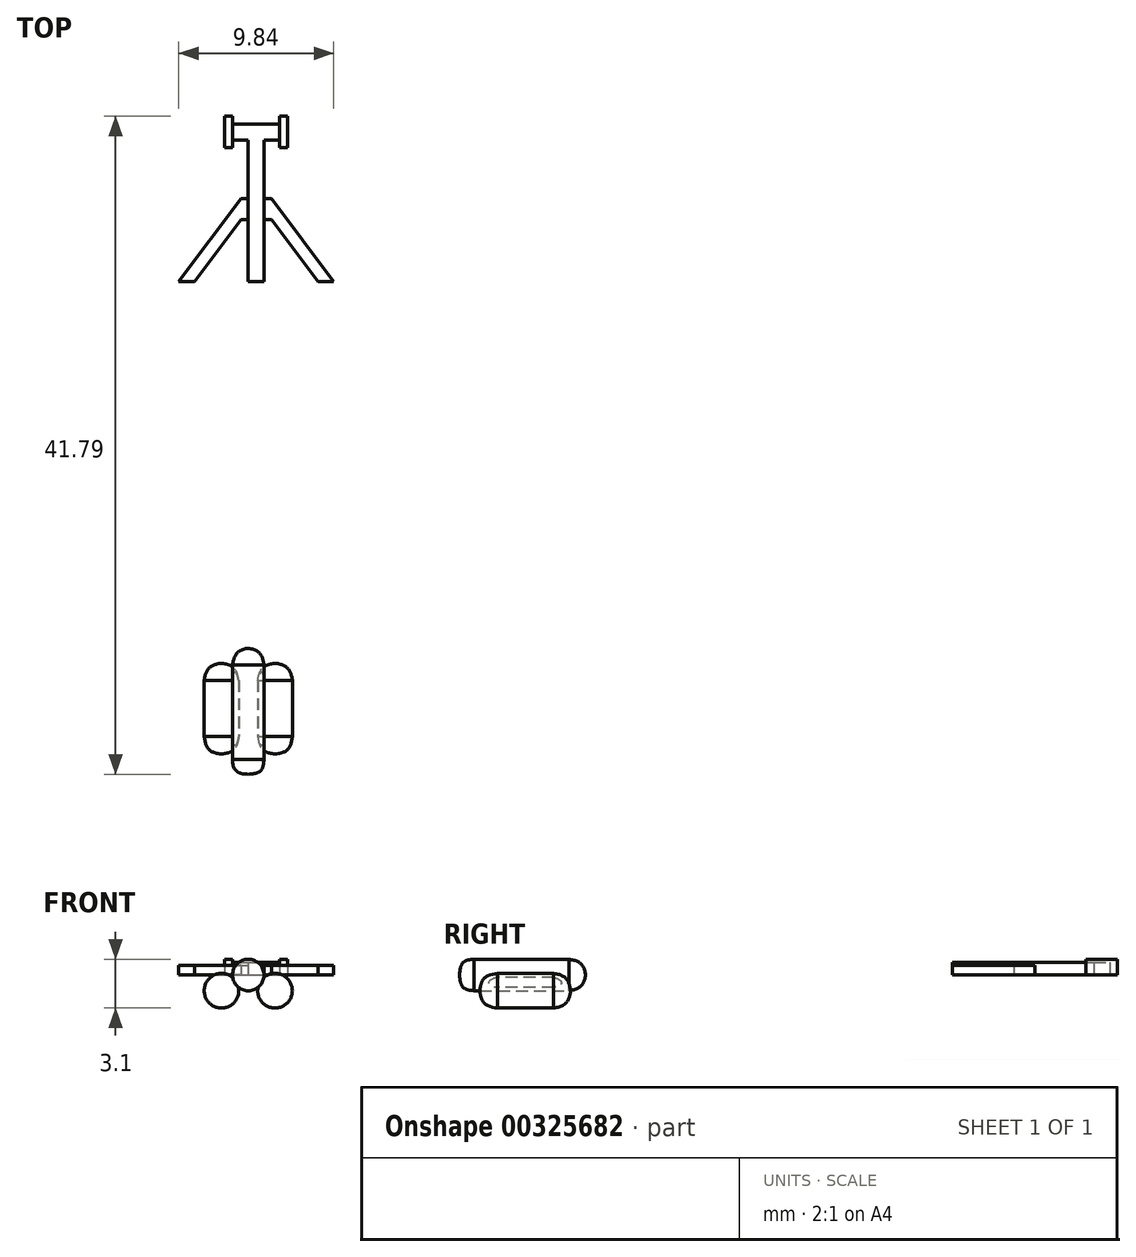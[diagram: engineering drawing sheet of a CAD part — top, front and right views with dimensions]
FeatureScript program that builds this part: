
annotation { "Feature Type Name" : "Feature", "Feature Type Description" : "" }
export const myFeature = defineFeature(function(context is Context, id is Id, definition is map)
    precondition{}
    {
        {
            var Q0;
            Q0=qCreatedBy(makeId("Top.planeOp"),FACE);
            var sketch = newSketch(context, id + "F0", { "sketchPlane" : qUnion([Q0])});
            skLineSegment(sketch, "E0.bottom", {"start": v(0, 0) * mm, "end": v(1, 0) * mm});
            skLineSegment(sketch, "E0.top", {"start": v(0, 10) * mm, "end": v(1, 10) * mm});
            skLineSegment(sketch, "E0.left", {"start": v(0, 0) * mm, "end": v(0, 10) * mm});
            skLineSegment(sketch, "E0.right", {"start": v(1, 0) * mm, "end": v(1, 10) * mm});
            skPoint(sketch, "E1", {"position": v(0.5, 10) * mm});
            skLineSegment(sketch, "E2.bottom", {"start": v(-1, 10) * mm, "end": v(2, 10) * mm});
            skLineSegment(sketch, "E2.top", {"start": v(-1, 9) * mm, "end": v(2, 9) * mm});
            skLineSegment(sketch, "E2.left", {"start": v(2, 10) * mm, "end": v(2, 9) * mm});
            skLineSegment(sketch, "E2.right", {"start": v(-1, 10) * mm, "end": v(-1, 9) * mm});
            skPoint(sketch, "E3", {"position": v(-1, 9.5) * mm});
            skPoint(sketch, "E4", {"position": v(2, 9.5) * mm});
            skLineSegment(sketch, "E5.bottom", {"start": v(-1.5, 10.5) * mm, "end": v(-1, 10.5) * mm});
            skLineSegment(sketch, "E5.top", {"start": v(-1.5, 8.5) * mm, "end": v(-1, 8.5) * mm});
            skLineSegment(sketch, "E5.left", {"start": v(-1.5, 10.5) * mm, "end": v(-1.5, 8.5) * mm});
            skLineSegment(sketch, "E5.right", {"start": v(-1, 10.5) * mm, "end": v(-1, 8.5) * mm});
            skLineSegment(sketch, "E6", {"start": v(0.5, 10) * mm, "end": v(0.5, 10.52) * mm, "construction": true});
            skLineSegment(sketch, "E7.MirrorCS", {"start": v(2, 10.5) * mm, "end": v(2, 8.5) * mm});
            skLineSegment(sketch, "E8.MirrorCS", {"start": v(2.5, 10.5) * mm, "end": v(2, 10.5) * mm});
            skLineSegment(sketch, "E9.MirrorCS", {"start": v(2.5, 10.5) * mm, "end": v(2.5, 8.5) * mm});
            skLineSegment(sketch, "E10.MirrorCS", {"start": v(2.5, 8.5) * mm, "end": v(2, 8.5) * mm});
            skSolve(sketch);
        }
        {
            var Q0;
            Q0=qSketchRegion(id+"F0",true);
            extrude(context, id + "F1", {"entities" : qUnion([Q0]), "depth" : .8 * mm});
        }
        {
            var Q0;
            {var subQ0=sQuery(id+"F0.wireOp",EDGE,"E8.MirrorCS");Q0=makeQuery(id+"F0.imprint","IMPRINT",FACE,{"disambiguationData":[TD([[makeQuery(id+"F0.imprint","IMPRINT",EDGE,{"derivedFrom":subQ0}),1.0]])]});}
            var Q1;
            {var subQ2=sQuery(id+"F0.wireOp",EDGE,"E5.bottom");Q1=makeQuery(id+"F0.imprint","IMPRINT",FACE,{"disambiguationData":[TD([[makeQuery(id+"F0.imprint","IMPRINT",EDGE,{"derivedFrom":subQ2}),-1.0]])]});}
            extrude(context, id + "F2", {"entities" : qUnion([Q0, Q1]), "operationType" : NewBodyOperationType.ADD, "depth" : 1 * mm});
        }
        {
            var Q0;
            Q0=qCreatedBy(makeId("Top.planeOp"),FACE);
            var sketch = newSketch(context, id + "F3", { "sketchPlane" : qUnion([Q0])});
            skPoint(sketch, "E11.0", {"position": v(0.5, 10) * mm});
            skLineSegment(sketch, "E12", {"start": v(0.5, 10) * mm, "end": v(0.5, 3.34) * mm, "construction": true});
            skLineSegment(sketch, "E13", {"start": v(-2.53, 3.75) * mm, "end": v(-2.04, 3.75) * mm});
            skLineSegment(sketch, "E14", {"start": v(-2.53, 3.75) * mm, "end": v(-3.53, 3.75) * mm});
            skPoint(sketch, "E15", {"position": v(-3.03, 3.75) * mm});
            skPoint(sketch, "E16", {"position": v(-2.04, 3.75) * mm});
            skLineSegment(sketch, "E17.MirrorCS", {"start": v(3.53, 3.75) * mm, "end": v(4.53, 3.75) * mm});
            skPoint(sketch, "E18.end.orphan", {"position": v(0.5, 5.72) * mm});
            skPoint(sketch, "E19.orphan", {"position": v(-1.54, 3.75) * mm});
            skPoint(sketch, "E20.MirrorCS.start.orphan", {"position": v(2.54, 3.75) * mm});
            skPoint(sketch, "E21.MirrorCS.start.orphan", {"position": v(3.53, 3.75) * mm});
            skLineSegment(sketch, "E22.MirrorCS", {"start": v(3.53, 3.75) * mm, "end": v(3.04, 3.75) * mm});
            skPoint(sketch, "E23.start.orphan", {"position": v(0.5, 6.67) * mm});
            skLineSegment(sketch, "E24", {"start": v(0.5, 7.15) * mm, "end": v(-0.47, 7.15) * mm});
            skLineSegment(sketch, "E25", {"start": v(-0.47, 7.15) * mm, "end": v(-3.03, 3.75) * mm});
            skLineSegment(sketch, "E26", {"start": v(-2.04, 3.75) * mm, "end": v(-0.2, 6.18) * mm});
            skLineSegment(sketch, "E27", {"start": v(-0.2, 6.18) * mm, "end": v(0.5, 6.2) * mm});
            skPoint(sketch, "E28.MirrorCS.end.orphan", {"position": v(0.5, 7.15) * mm});
            skPoint(sketch, "E28.MirrorCS.start.orphan", {"position": v(4.03, 3.75) * mm});
            skPoint(sketch, "E29.MirrorCS.end.orphan", {"position": v(0.5, 6.2) * mm});
            skPoint(sketch, "E29.MirrorCS.start.orphan", {"position": v(3.04, 3.75) * mm});
            skLineSegment(sketch, "E30.MirrorCS", {"start": v(0.5, 7.15) * mm, "end": v(1.47, 7.15) * mm});
            skLineSegment(sketch, "E31.MirrorCS", {"start": v(1.47, 7.15) * mm, "end": v(4.03, 3.75) * mm});
            skLineSegment(sketch, "E32.MirrorCS", {"start": v(3.04, 3.75) * mm, "end": v(1.2, 6.18) * mm});
            skLineSegment(sketch, "E33.MirrorCS", {"start": v(1.2, 6.18) * mm, "end": v(0.5, 6.2) * mm});
            skLineSegment(sketch, "E34", {"start": v(0.5, 5.26) * mm, "end": v(-0.47, 5.26) * mm});
            skLineSegment(sketch, "E35", {"start": v(-0.47, 5.26) * mm, "end": v(-4.42, 0) * mm});
            skLineSegment(sketch, "E36", {"start": v(-4.42, 0) * mm, "end": v(-3.42, 0) * mm});
            skLineSegment(sketch, "E37", {"start": v(-3.42, 0) * mm, "end": v(-0.47, 3.93) * mm});
            skLineSegment(sketch, "E38", {"start": v(-0.47, 3.93) * mm, "end": v(0.5, 3.93) * mm});
            skLineSegment(sketch, "E39.MirrorCS", {"start": v(0.5, 5.26) * mm, "end": v(1.47, 5.26) * mm});
            skLineSegment(sketch, "E40.MirrorCS", {"start": v(1.47, 5.26) * mm, "end": v(5.42, 0) * mm});
            skLineSegment(sketch, "E41.MirrorCS", {"start": v(5.42, 0) * mm, "end": v(4.42, 0) * mm});
            skLineSegment(sketch, "E42.MirrorCS", {"start": v(4.42, 0) * mm, "end": v(1.47, 3.93) * mm});
            skLineSegment(sketch, "E43.MirrorCS", {"start": v(1.47, 3.93) * mm, "end": v(0.5, 3.93) * mm});
            skSolve(sketch);
        }
        {
            var Q0;
            Q0=makeQuery(id+"F3.imprint","IMPRINT",FACE,{"disambiguationData":[TD([[makeQuery(id+"F3.imprint","IMPRINT",EDGE,{"derivedFrom":sQuery(id+"F3.wireOp",EDGE,"E34")}),1.0]])]});
            extrude(context, id + "F4", {"entities" : qUnion([Q0]), "operationType" : NewBodyOperationType.ADD, "depth" : .6 * mm});
        }
        {
            var Q0;
            Q0=qCreatedBy(makeId("Top.planeOp"),FACE);
            var sketch = newSketch(context, id + "F5", { "sketchPlane" : qUnion([Q0])});
            skLineSegment(sketch, "E44", {"start": v(0, -23.3) * mm, "end": v(0, -31.3) * mm});
            skLineSegment(sketch, "E45", {"start": v(1, -23.3) * mm, "end": v(1, -31.3) * mm});
            skFitSpline(sketch, "E46", {"points": [v(0, -31.3) * mm, v(1, -30.36) * mm], "startDerivative": vector(2.5, 0.13) * mm, "endDerivative": vector(0.12, 1.93) * mm});
            skFitSpline(sketch, "E47", {"points": [v(0, -23.3) * mm, v(1, -24.36) * mm], "startDerivative": vector(2.31, -0.2) * mm, "endDerivative": vector(0.21, -1.56) * mm});
            skSolve(sketch);
        }
        {
            var Q0;
            Q0=qSketchRegion(id+"F5",true);
            var Q1;
            Q1=sQuery(id+"F5.wireOp",EDGE,"E44");
            revolve(context, id + "F6", {"entities" : qUnion([Q0]), "axis" : qUnion([Q1]), "revolveType" : RevolveType.FULL});
        }
        {
            var Q0;
            Q0=qCreatedBy(makeId("Top.planeOp"),FACE);
            cPlane(context, id + "F7", {"entities" : qUnion([Q0]), "cplaneType" : CPlaneType.OFFSET, "offset" : 1 * mm, "oppositeDirection" : true, "width" : 150 * mm, "height" : 150 * mm});
        }
        {
            var Q0;
            Q0=qCreatedBy(id+"F7.planeOp",FACE);
            var sketch = newSketch(context, id + "F8", { "sketchPlane" : qUnion([Q0])});
            skLineSegment(sketch, "E48", {"start": v(0, -24.24) * mm, "end": v(0, -30) * mm});
            skLineSegment(sketch, "E49", {"start": v(0, -30) * mm, "end": v(1.7, -30) * mm});
            skLineSegment(sketch, "E50", {"start": v(1.7, -30) * mm, "end": v(1.7, -24.24) * mm});
            skLineSegment(sketch, "E51", {"start": v(1.7, -24.24) * mm, "end": v(2.8, -24.24) * mm});
            skLineSegment(sketch, "E52", {"start": v(2.8, -24.24) * mm, "end": v(2.8, -30) * mm});
            skLineSegment(sketch, "E53", {"start": v(2.8, -30) * mm, "end": v(1.7, -30) * mm});
            skFitSpline(sketch, "E54", {"points": [v(1.7, -24.24) * mm, v(2.8, -25.32) * mm], "startDerivative": vector(2.2, -0.25) * mm, "endDerivative": vector(0.28, -2.11) * mm});
            skFitSpline(sketch, "E55", {"points": [v(1.7, -30) * mm, v(2.8, -28.88) * mm], "startDerivative": vector(2.58, 0.22) * mm, "endDerivative": vector(0.3, 2.18) * mm});
            skLineSegment(sketch, "E56.MirrorCS", {"start": v(-1.7, -30) * mm, "end": v(-1.7, -24.24) * mm});
            skFitSpline(sketch, "E57.MirrorCS", {"points": [v(-1.7, -30) * mm, v(-2.8, -28.88) * mm], "startDerivative": vector(-2.58, 0.22) * mm, "endDerivative": vector(-0.3, 2.18) * mm});
            skLineSegment(sketch, "E58.MirrorCS", {"start": v(-2.8, -24.24) * mm, "end": v(-2.8, -30) * mm});
            skFitSpline(sketch, "E59.MirrorCS", {"points": [v(-1.7, -24.24) * mm, v(-2.8, -25.32) * mm], "startDerivative": vector(-2.2, -0.25) * mm, "endDerivative": vector(-0.28, -2.11) * mm});
            skSolve(sketch);
        }
        {
            var Q0;
            Q0=makeQuery(id+"F8.imprint","IMPRINT",FACE,{"disambiguationData":[TD([[makeQuery(id+"F8.imprint","IMPRINT",EDGE,{"derivedFrom":sQuery(id+"F8.wireOp",EDGE,"E50")}),-1.0]])]});
            var Q1;
            Q1=sQuery(id+"F8.wireOp",EDGE,"E50");
            revolve(context, id + "F9", {"operationType" : NewBodyOperationType.ADD, "entities" : qUnion([Q0]), "axis" : qUnion([Q1]), "revolveType" : RevolveType.FULL});
        }
        {
            var Q0;
            Q0=makeQuery(id+"F8.imprint","IMPRINT",FACE,{"disambiguationData":[TD([[makeQuery(id+"F8.imprint","IMPRINT",EDGE,{"derivedFrom":sQuery(id+"F8.wireOp",EDGE,"E56.MirrorCS")}),1.0]])]});
            var Q1;
            Q1=sQuery(id+"F8.wireOp",EDGE,"E56.MirrorCS");
            revolve(context, id + "F10", {"operationType" : NewBodyOperationType.ADD, "entities" : qUnion([Q0]), "axis" : qUnion([Q1]), "revolveType" : RevolveType.FULL});
        }
    });
